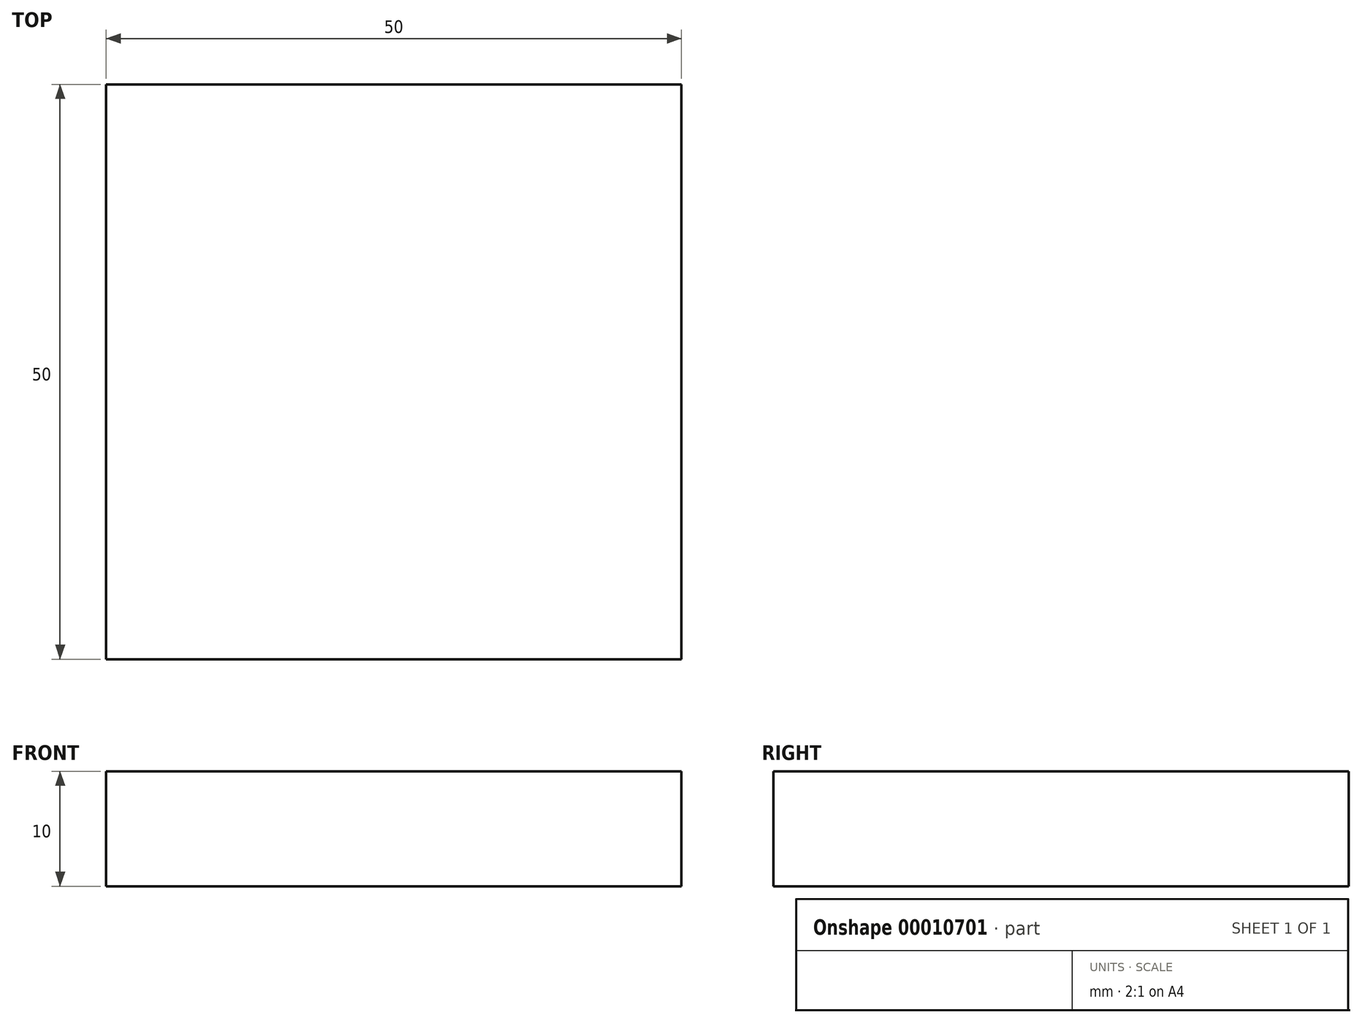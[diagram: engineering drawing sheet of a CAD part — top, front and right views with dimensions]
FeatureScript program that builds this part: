
annotation { "Feature Type Name" : "Feature", "Feature Type Description" : "" }
export const myFeature = defineFeature(function(context is Context, id is Id, definition is map)
    precondition{}
    {
        {
            var Q0;
            Q0=qCreatedBy(makeId("Top.planeOp"),FACE);
            var sketch = newSketch(context, id + "F1", { "sketchPlane" : qUnion([Q0])});
            skLineSegment(sketch, "E0.rect.bottom", {"start": v(25, 25) * mm, "end": v(-25, 25) * mm});
            skLineSegment(sketch, "E0.rect.top", {"start": v(25, -25) * mm, "end": v(-25, -25) * mm});
            skLineSegment(sketch, "E0.rect.left", {"start": v(25, 25) * mm, "end": v(25, -25) * mm});
            skLineSegment(sketch, "E0.rect.right", {"start": v(-25, 25) * mm, "end": v(-25, -25) * mm});
            skPoint(sketch, "E0.rect.middle", {"position": v(0, 0) * mm});
            skPoint(sketch, "E1.rect.bottom.start.orphan", {"position": v(25.55, 25.55) * mm});
            skPoint(sketch, "E1.rect.top.start.orphan", {"position": v(25.55, -25.55) * mm});
            skPoint(sketch, "E1.rect.right.end.orphan", {"position": v(-25.55, -25.55) * mm});
            skPoint(sketch, "E1.rect.right.start.orphan", {"position": v(-25.55, 25.55) * mm});
            skSolve(sketch);
        }
        {
            var Q0;
            Q0=makeQuery(id+"F1.imprint","IMPRINT",FACE,{"disambiguationData":[TD([[makeQuery(id+"F1.imprint","IMPRINT",EDGE,{"derivedFrom":sQuery(id+"F1.wireOp",EDGE,"E0.rect.bottom")}),-1.0]])]});
            var Q1;
            Q1=makeQuery(id+"F1.imprint","IMPRINT",FACE,{"disambiguationData":[TD([[makeQuery(id+"F1.imprint","IMPRINT",EDGE,{"derivedFrom":sQuery(id+"F1.wireOp",EDGE,"E0.rect.bottom")}),1.0]])]});
            extrude(context, id + "F0", {"entities" : qUnion([Q0, Q1]), "depth" : 10 * mm});
        }
    });
